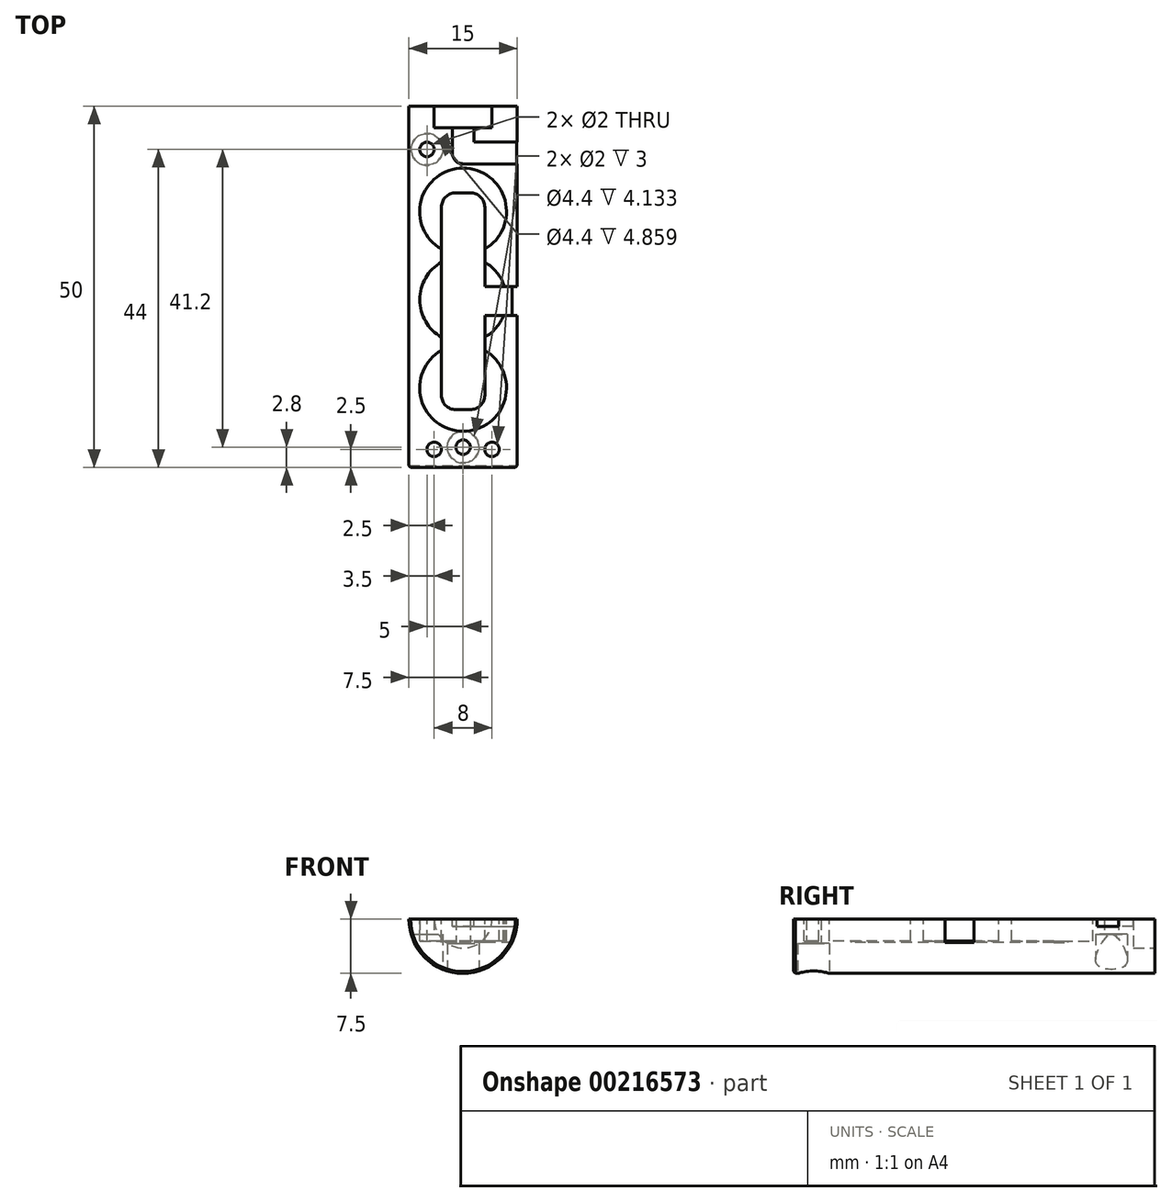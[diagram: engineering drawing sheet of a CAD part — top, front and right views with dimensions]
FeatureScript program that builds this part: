
annotation { "Feature Type Name" : "Feature", "Feature Type Description" : "" }
export const myFeature = defineFeature(function(context is Context, id is Id, definition is map)
    precondition{}
    {
        {
            var Q0;
            Q0=qCreatedBy(makeId("Front.planeOp"),FACE);
            var sketch = newSketch(context, id + "F0", { "sketchPlane" : qUnion([Q0])});
            skArc(sketch, "E0", {"start": v(-7.5, 0) * mm, "mid": v(0, -7.5) * mm, "end": v(7.5, 0) * mm});
            skLineSegment(sketch, "E1", {"start": v(-7.5, 0) * mm, "end": v(7.5, 0) * mm});
            skSolve(sketch);
        }
        {
            var Q0;
            Q0 = qSketchRegion(id + "F0", true);
            extrude(context, id + "F1", {"entities" : qUnion([Q0]), "depth" : 50 * mm});
        }
        {
            var Q0;
            Q0=makeQuery(id+"F1.opExtrude","SWEPT_FACE",FACE,{"disambiguationData":[OSD([sQuery(id+"F0.wireOp",EDGE,"E1")])]});
            var sketch = newSketch(context, id + "F2", { "sketchPlane" : qUnion([Q0])});
            skCircle(sketch, "E2", {"center": v(0, -39) * mm, "radius": 6 * mm});
            skCircle(sketch, "E3.0.1.0", {"center": v(0, -26.8) * mm, "radius": 6 * mm});
            skCircle(sketch, "E3.0.2.0", {"center": v(0, -14.6) * mm, "radius": 6 * mm});
            skLineSegment(sketch, "E3.direction1", {"start": v(0, -39) * mm, "end": v(25, -39) * mm, "construction": true});
            skLineSegment(sketch, "E3.direction2", {"start": v(0, -39) * mm, "end": v(0, -26.8) * mm, "construction": true});
            skSolve(sketch);
        }
        {
            var Q0;
            Q0 = qSketchRegion(id + "F2", true);
            extrude(context, id + "F3", {"entities" : qUnion([Q0]), "operationType" : NewBodyOperationType.REMOVE, "oppositeDirection" : true, "depth" : 3 * mm});
        }
        {
            var Q0;
            Q0=makeQuery(id+"F1.opExtrude","CAP_FACE",FACE,{"disambiguationData":[OSD([sQuery(id+"F0.wireOp",EDGE,"E0"),sQuery(id+"F0.wireOp",EDGE,"E1")])],"isStart":true});
            var sketch = newSketch(context, id + "F4", { "sketchPlane" : qUnion([Q0])});
            skCircle(sketch, "E4", {"center": v(0, 0) * mm, "radius": 4 * mm});
            skSolve(sketch);
        }
        {
            var Q0;
            Q0 = qSketchRegion(id + "F4", true);
            extrude(context, id + "F5", {"entities" : qUnion([Q0]), "operationType" : NewBodyOperationType.REMOVE, "oppositeDirection" : true, "depth" : 3 * mm});
        }
        {
            var Q0;
            Q0=makeQuery(id+"F1.opExtrude","SWEPT_FACE",FACE,{"disambiguationData":[OSD([sQuery(id+"F0.wireOp",EDGE,"E1")])]});
            var sketch = newSketch(context, id + "F6", { "sketchPlane" : qUnion([Q0])});
            skLineSegment(sketch, "E5.bottom", {"start": v(1, -12) * mm, "end": v(-1, -12) * mm});
            skLineSegment(sketch, "E5.top", {"start": v(1, -42) * mm, "end": v(-1, -42) * mm});
            skLineSegment(sketch, "E5.left", {"start": v(3, -14) * mm, "end": v(3, -40) * mm});
            skLineSegment(sketch, "E5.right", {"start": v(-3, -14) * mm, "end": v(-3, -40) * mm});
            skPoint(sketch, "E6.visualSharp", {"position": v(3, -12) * mm});
            skArc(sketch, "E6.filletArc", {"start": v(3, -14) * mm, "mid": v(2.41, -12.59) * mm, "end": v(1, -12) * mm});
            skPoint(sketch, "E7.visualSharp", {"position": v(-3, -12) * mm});
            skArc(sketch, "E7.filletArc", {"start": v(-1, -12) * mm, "mid": v(-2.41, -12.59) * mm, "end": v(-3, -14) * mm});
            skPoint(sketch, "E8.visualSharp", {"position": v(3, -42) * mm});
            skArc(sketch, "E8.filletArc", {"start": v(1, -42) * mm, "mid": v(2.41, -41.41) * mm, "end": v(3, -40) * mm});
            skPoint(sketch, "E9.visualSharp", {"position": v(-3, -42) * mm});
            skArc(sketch, "E9.filletArc", {"start": v(-3, -40) * mm, "mid": v(-2.41, -41.41) * mm, "end": v(-1, -42) * mm});
            skLineSegment(sketch, "E10.bottom", {"start": v(8, -25) * mm, "end": v(3, -25) * mm});
            skLineSegment(sketch, "E10.top", {"start": v(8, -29) * mm, "end": v(3, -29) * mm});
            skLineSegment(sketch, "E10.left", {"start": v(8, -25) * mm, "end": v(8, -29) * mm});
            skLineSegment(sketch, "E10.right", {"start": v(3, -25) * mm, "end": v(3, -29) * mm});
            skSolve(sketch);
        }
        {
            var Q0;
            Q0 = qSketchRegion(id + "F6", true);
            extrude(context, id + "F7", {"entities" : qUnion([Q0]), "operationType" : NewBodyOperationType.REMOVE, "oppositeDirection" : true, "depth" : 3.2 * mm});
        }
        {
            var Q0;
            Q0=qCreatedBy(makeId("Top.planeOp"),FACE);
            cPlane(context, id + "F8", {"entities" : qUnion([Q0]), "cplaneType" : CPlaneType.OFFSET, "offset" : 7.5 * mm, "oppositeDirection" : true, "width" : 150 * mm, "height" : 150 * mm});
        }
        {
            var Q0;
            Q0=qCreatedBy(id+"F8.planeOp",FACE);
            var sketch = newSketch(context, id + "F9", { "sketchPlane" : qUnion([Q0])});
            skPoint(sketch, "E11", {"position": v(0, -47.2) * mm});
            skSolve(sketch);
        }
        {
            var Q0;
            Q0=sQuery(id+"F9.wireOp",VERTEX,"E11");
            var Q1;
            Q1=makeQuery(id+"F1.opExtrude","SWEPT_BODY",BODY,{"disambiguationData":[OSD([sQuery(id+"F0.wireOp",EDGE,"E0"),sQuery(id+"F0.wireOp",EDGE,"E1")])]});
            hole(context, id + "F10", {"style" : HoleStyle.C_BORE, "endStyle" : HoleEndStyle.BLIND, "oppositeDirection" : true, "holeDiameter" : 2 * mm, "cBoreDiameter" : 4.4 * mm, "cBoreDepth" : 3.8 * mm, "holeDepth" : 8 * mm, "locations" : qUnion([Q0]), "scope" : qUnion([Q1])});
        }
        {
            var Q0;
            Q0=qCreatedBy(id+"F8.planeOp",FACE);
            var sketch = newSketch(context, id + "F11", { "sketchPlane" : qUnion([Q0])});
            skPoint(sketch, "E12", {"position": v(-5, -6) * mm});
            skSolve(sketch);
        }
        {
            var Q0;
            Q0=sQuery(id+"F11.wireOp",VERTEX,"E12");
            var Q1;
            Q1=makeQuery(id+"F1.opExtrude","SWEPT_BODY",BODY,{"disambiguationData":[OSD([sQuery(id+"F0.wireOp",EDGE,"E0"),sQuery(id+"F0.wireOp",EDGE,"E1")])]});
            hole(context, id + "F12", {"style" : HoleStyle.C_BORE, "endStyle" : HoleEndStyle.BLIND, "oppositeDirection" : true, "holeDiameter" : 2 * mm, "cBoreDiameter" : 4.4 * mm, "cBoreDepth" : 0 * mm, "holeDepth" : 8 * mm, "locations" : qUnion([Q0]), "scope" : qUnion([Q1])});
        }
        {
            var Q0;
            Q0=makeQuery(id+"F1.opExtrude","SWEPT_FACE",FACE,{"disambiguationData":[OSD([sQuery(id+"F0.wireOp",EDGE,"E1")])]});
            var sketch = newSketch(context, id + "F13", { "sketchPlane" : qUnion([Q0])});
            skLineSegment(sketch, "E13.bottom", {"start": v(-1.5, -3) * mm, "end": v(1.5, -3) * mm});
            skLineSegment(sketch, "E13.top", {"start": v(-1.5, -8) * mm, "end": v(1.5, -8) * mm});
            skLineSegment(sketch, "E13.left", {"start": v(-1.5, -3) * mm, "end": v(-1.5, -8) * mm});
            skLineSegment(sketch, "E13.right", {"start": v(1.5, -3) * mm, "end": v(1.5, -5) * mm});
            skLineSegment(sketch, "E14.bottom", {"start": v(1.5, -8) * mm, "end": v(8.57, -8) * mm});
            skLineSegment(sketch, "E14.top", {"start": v(1.5, -5) * mm, "end": v(8.57, -5) * mm});
            skLineSegment(sketch, "E14.right", {"start": v(8.57, -8) * mm, "end": v(8.57, -5) * mm});
            skSolve(sketch);
        }
        {
            var Q0;
            Q0 = qSketchRegion(id + "F13", true);
            extrude(context, id + "F14", {"entities" : qUnion([Q0]), "operationType" : NewBodyOperationType.REMOVE, "oppositeDirection" : true, "depth" : 1 * mm});
        }
        {
            var Q0;
            Q0=makeQuery(id+"F14.boolean.opBoolean","COPY",EDGE,{"derivedFrom":makeQuery(id+"F14.opExtrude","SWEPT_EDGE",EDGE,{"disambiguationData":[OSD([sQuery(id+"F13.wireOp",EDGE,"E13.top"),sQuery(id+"F13.wireOp",EDGE,"E13.left")])]})});
            fillet(context, id + "F15", {"entities" : qUnion([Q0]), "radius" : 1.5 * mm, "tangentPropagation" : true, "allowEdgeOverflow" : false});
        }
        {
            var Q0;
            Q0=makeQuery(id+"F1.opExtrude","CAP_EDGE",EDGE,{"disambiguationData":[OSD([sQuery(id+"F0.wireOp",EDGE,"E0")])],"isStart":false});
            chamfer(context, id + "F16", {"entities" : qUnion([Q0]), "width" : 0.25 * mm, "tangentPropagation" : true});
        }
        {
            var Q0;
            {var subQ1=sQuery(id+"F2.wireOp",EDGE,"E2");var subQ14=sQuery(id+"F0.wireOp",EDGE,"E1");Q0=makeQuery(id+"F14.boolean.opBoolean","SPLIT",FACE,{"disambiguationData":[TD([makeQuery(id+"F3.boolean.opBoolean","COPY",FACE,{"derivedFrom":makeQuery(id+"F3.opExtrude","SWEPT_FACE",FACE,{"disambiguationData":[OSD([subQ1])]})})])],"derivedFrom":makeQuery(id+"F1.opExtrude","SWEPT_FACE",FACE,{"disambiguationData":[OSD([subQ14])]})});}
            var sketch = newSketch(context, id + "F17", { "sketchPlane" : qUnion([Q0])});
            skCircle(sketch, "E15", {"center": v(-4, -47.5) * mm, "radius": 1 * mm});
            skCircle(sketch, "E16", {"center": v(4, -47.5) * mm, "radius": 1 * mm});
            skSolve(sketch);
        }
        {
            var Q0;
            Q0 = qSketchRegion(id + "F17", true);
            extrude(context, id + "F18", {"entities" : qUnion([Q0]), "operationType" : NewBodyOperationType.REMOVE, "oppositeDirection" : true, "depth" : 3 * mm});
        }
    });
